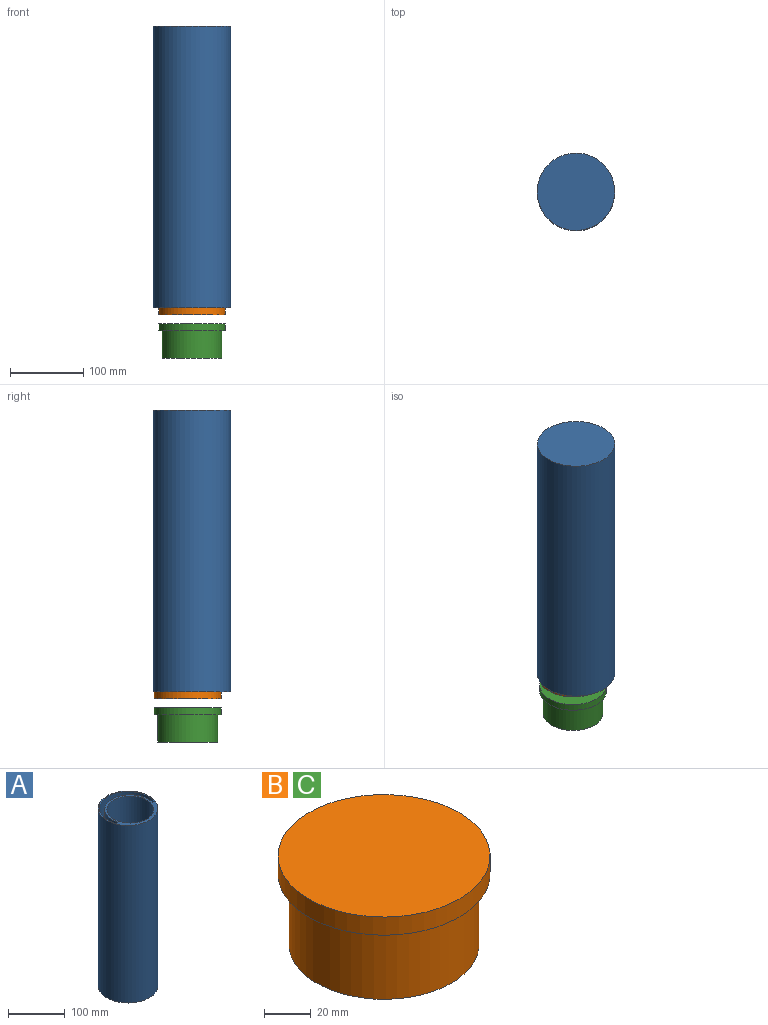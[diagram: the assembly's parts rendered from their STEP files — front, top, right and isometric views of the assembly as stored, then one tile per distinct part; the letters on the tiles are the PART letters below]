
ASSEMBLY  parts=3 mates=4
PART A: 11 faces, bbox 105.7x105.7x384.2 mm
  f0: cylinder r=45.09mm len=368.3mm, axis (0,0,-1), area 61162.3mm2, adj f2,f4,f6,f8
  f1: cylinder r=41.27mm len=368.3mm, axis (0,0,-1), area 95514.4mm2, adj f6,f8
  f2: plane 381x4.15mm, normal (0,1,0), area 1579.7mm2, adj f0,f3,f6,f7,f9
  f3: cylinder r=50.8mm len=381mm, axis (0,0,-1), area 74646.3mm2, adj f2,f4,f6,f9
  f4: plane 381x4.15mm, normal (0,1,0), area 1579.7mm2, adj f0,f3,f6,f7,f9
  f5: cylinder r=52.83mm len=384.18mm, axis (0,0,-1), area 127528.1mm2, adj f6,f10
  f6: plane 105.66x105.66mm, normal (0,0,1), area 1861.9mm2, adj f0,f1,f2,f3,f4,f5
  f7: cylinder r=45.09mm len=86.88mm, axis (0,0,-1), area 1488.6mm2, adj f2,f4,f8,f9
  f8: plane 90.17x90.17mm, normal (0,0,-1), area 1033.7mm2, adj f0,f1,f7
  f9: plane 101.6x101.6mm, normal (0,0,1), area 7940.6mm2, adj f2,f3,f4,f7
  f10: plane 105.66x105.66mm, normal (0,0,-1), area 8768.9mm2, adj f5
PART B: 5 faces, bbox 91.1x91.1x46.6 mm
  f0: cylinder r=40.77mm len=81.53mm, axis (0,0,1), area 9498.9mm2, adj f1,f4
  f1: plane 81.53x81.53mm, normal (0,0,-1), area 5221.2mm2, adj f0
  f2: cylinder r=45.53mm len=91.06mm, axis (0,0,-1), area 2724.8mm2, adj f3,f4
  f3: plane 91.06x91.06mm, normal (0,0,1), area 6512.3mm2, adj f2
  f4: plane 91.06x91.06mm, normal (0,0,-1), area 1291.2mm2, adj f0,f2
PART C: same geometry as B
PLACE A rot(axis=(1,0,0),180deg) t=(-170.25,-214.8,425.7)mm
PLACE B rot(axis=(-0.71,-0.71,0),180deg) t=(-170.25,-209.08,235.2)mm
PLACE C t=(-170.25,-209.08,203.45)mm
MATE cylindrical B.f0 <-> C.f2  axis (0,0,-1) through (-170.25,-209.08,235.2)mm
MATE planar B.f2 <-> C.f2  axis (0,0,-1) through (-170.25,-209.08,225.68)mm
MATE cylindrical A.f1 <-> C.f0  axis (0,0,1) through (-170.25,-209.08,419.35)mm
MATE planar B.f2 <-> A.f6  axis (0,0,1) through (-170.25,-209.08,235.2)mm
